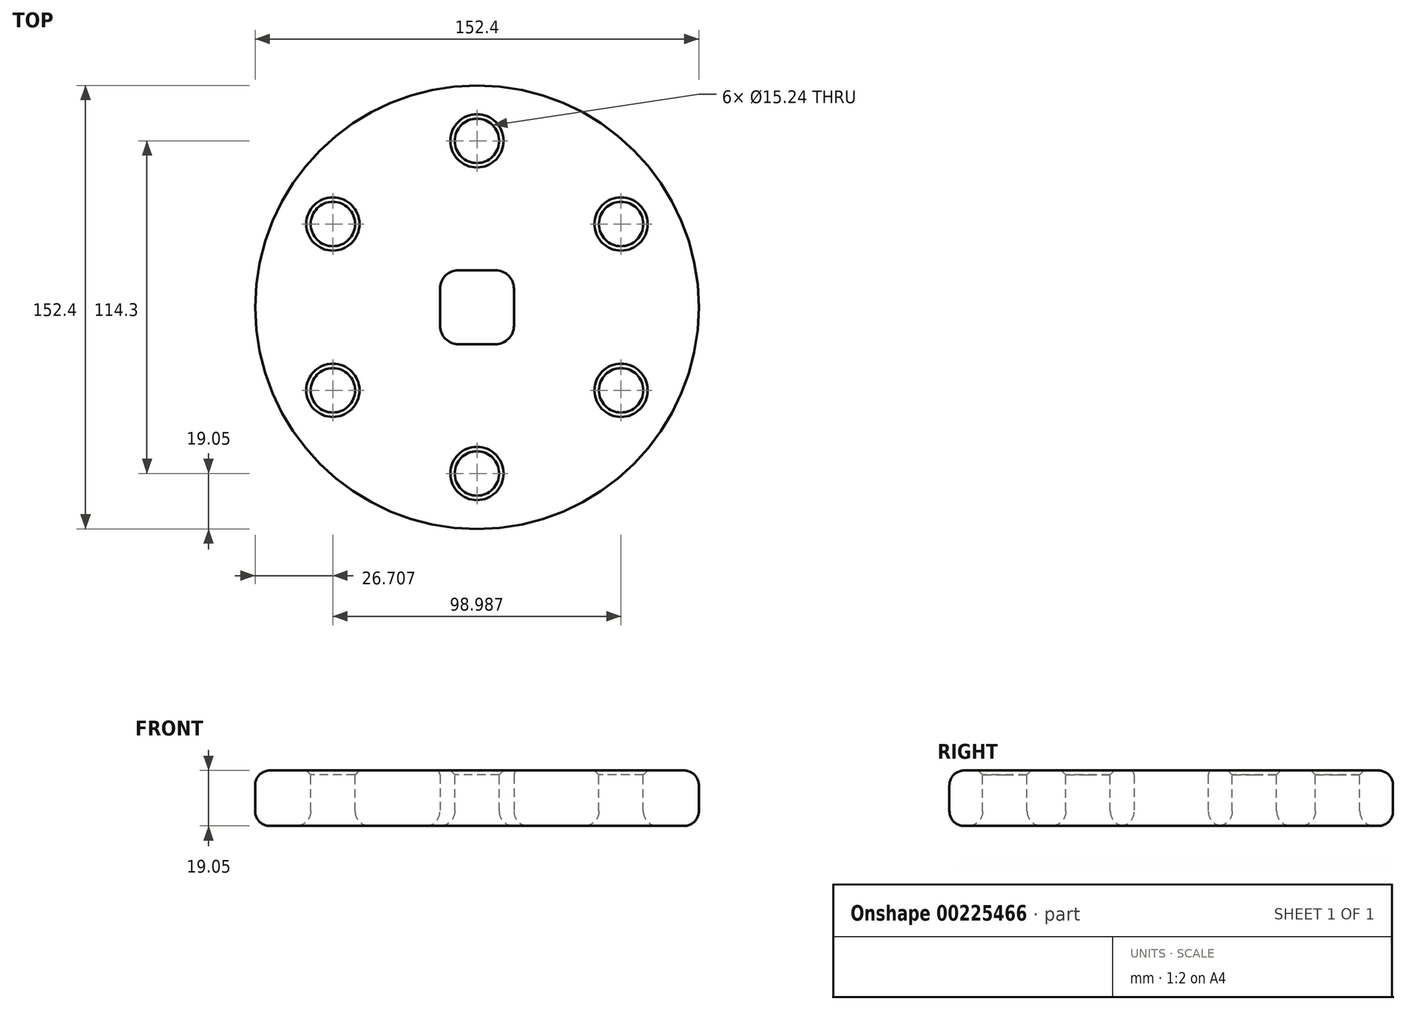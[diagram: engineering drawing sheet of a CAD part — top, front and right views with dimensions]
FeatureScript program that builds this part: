
annotation { "Feature Type Name" : "Feature", "Feature Type Description" : "" }
export const myFeature = defineFeature(function(context is Context, id is Id, definition is map)
    precondition{}
    {
        {
            var Q0;
            Q0=qCreatedBy(makeId("Top.planeOp"),FACE);
            var sketch = newSketch(context, id + "F0", { "sketchPlane" : qUnion([Q0])});
            skCircle(sketch, "E0", {"center": v(0, 0) * mm, "radius": 76.2 * mm});
            skCircle(sketch, "E1", {"center": v(0, 0) * mm, "radius": 57.15 * mm, "construction": true});
            skCircle(sketch, "E2", {"center": v(0, 57.15) * mm, "radius": 7.62 * mm});
            skCircle(sketch, "E3.1.0", {"center": v(-49.5, 28.58) * mm, "radius": 7.62 * mm});
            skCircle(sketch, "E3.2.0", {"center": v(-49.5, -28.57) * mm, "radius": 7.62 * mm});
            skCircle(sketch, "E3.3.0", {"center": v(0, -57.15) * mm, "radius": 7.62 * mm});
            skCircle(sketch, "E3.4.0", {"center": v(49.5, -28.58) * mm, "radius": 7.62 * mm});
            skCircle(sketch, "E3.5.0", {"center": v(49.5, 28.58) * mm, "radius": 7.62 * mm});
            skSolve(sketch);
        }
        {
            var Q0;
            Q0 = qSketchRegion(id + "F0", true);
            extrude(context, id + "F1", {"entities" : qUnion([Q0]), "oppositeDirection" : true, "depth" : 19.05 * mm});
        }
        {
            var Q0;
            Q0=makeQuery(id+"F1.opExtrude","CAP_FACE",FACE,{"disambiguationData":[OSD([sQuery(id+"F0.wireOp",EDGE,"E0"),sQuery(id+"F0.wireOp",EDGE,"E2"),sQuery(id+"F0.wireOp",EDGE,"E3.1.0"),sQuery(id+"F0.wireOp",EDGE,"E3.2.0"),sQuery(id+"F0.wireOp",EDGE,"E3.3.0"),sQuery(id+"F0.wireOp",EDGE,"E3.4.0"),sQuery(id+"F0.wireOp",EDGE,"E3.5.0")])],"isStart":false});
            var sketch = newSketch(context, id + "F2", { "sketchPlane" : qUnion([Q0])});
            skLineSegment(sketch, "E4.bottom", {"start": v(6.35, -12.7) * mm, "end": v(-6.35, -12.7) * mm});
            skLineSegment(sketch, "E4.top", {"start": v(6.35, 12.7) * mm, "end": v(-6.35, 12.7) * mm});
            skLineSegment(sketch, "E4.left", {"start": v(12.7, -6.35) * mm, "end": v(12.7, 6.35) * mm});
            skLineSegment(sketch, "E4.right", {"start": v(-12.7, -6.35) * mm, "end": v(-12.7, 6.35) * mm});
            skPoint(sketch, "E4.middle", {"position": v(0, 0) * mm});
            skPoint(sketch, "E5.visualSharp", {"position": v(-12.7, 12.7) * mm});
            skArc(sketch, "E5.filletArc", {"start": v(-6.35, 12.7) * mm, "mid": v(-10.84, 10.84) * mm, "end": v(-12.7, 6.35) * mm});
            skPoint(sketch, "E6.visualSharp", {"position": v(12.7, 12.7) * mm});
            skArc(sketch, "E6.filletArc", {"start": v(12.7, 6.35) * mm, "mid": v(10.84, 10.84) * mm, "end": v(6.35, 12.7) * mm});
            skPoint(sketch, "E7.visualSharp", {"position": v(12.7, -12.7) * mm});
            skArc(sketch, "E7.filletArc", {"start": v(6.35, -12.7) * mm, "mid": v(10.84, -10.84) * mm, "end": v(12.7, -6.35) * mm});
            skPoint(sketch, "E8.visualSharp", {"position": v(-12.7, -12.7) * mm});
            skArc(sketch, "E8.filletArc", {"start": v(-12.7, -6.35) * mm, "mid": v(-10.84, -10.84) * mm, "end": v(-6.35, -12.7) * mm});
            skSolve(sketch);
        }
        {
            var Q0;
            Q0 = qSketchRegion(id + "F2", true);
            extrude(context, id + "F3", {"entities" : qUnion([Q0]), "operationType" : NewBodyOperationType.REMOVE, "endBound" : BoundingType.THROUGH_ALL, "oppositeDirection" : true, "depth" : 25.4 * mm});
        }
        {
            var Q0;
            Q0=makeQuery(id+"F1.opExtrude","CAP_EDGE",EDGE,{"disambiguationData":[OSD([sQuery(id+"F0.wireOp",EDGE,"E3.1.0")])],"isStart":true});
            var Q1;
            Q1=makeQuery(id+"F1.opExtrude","CAP_EDGE",EDGE,{"disambiguationData":[OSD([sQuery(id+"F0.wireOp",EDGE,"E2")])],"isStart":true});
            var Q2;
            Q2=makeQuery(id+"F1.opExtrude","CAP_EDGE",EDGE,{"disambiguationData":[OSD([sQuery(id+"F0.wireOp",EDGE,"E3.5.0")])],"isStart":true});
            var Q3;
            Q3=makeQuery(id+"F1.opExtrude","CAP_EDGE",EDGE,{"disambiguationData":[OSD([sQuery(id+"F0.wireOp",EDGE,"E3.4.0")])],"isStart":true});
            var Q4;
            Q4=makeQuery(id+"F1.opExtrude","CAP_EDGE",EDGE,{"disambiguationData":[OSD([sQuery(id+"F0.wireOp",EDGE,"E3.3.0")])],"isStart":true});
            var Q5;
            Q5=makeQuery(id+"F1.opExtrude","CAP_EDGE",EDGE,{"disambiguationData":[OSD([sQuery(id+"F0.wireOp",EDGE,"E3.2.0")])],"isStart":true});
            chamfer(context, id + "F4", {"entities" : qUnion([Q0, Q1, Q2, Q3, Q4, Q5]), "width" : 1.52 * mm, "tangentPropagation" : true});
        }
        {
            var Q0;
            Q0=makeQuery(id+"F3.boolean.opBoolean","INTERSECT",EDGE,{"derivedFrom":[makeQuery(id+"F1.opExtrude","CAP_FACE",FACE,{"disambiguationData":[OSD([sQuery(id+"F0.wireOp",EDGE,"E0"),sQuery(id+"F0.wireOp",EDGE,"E2"),sQuery(id+"F0.wireOp",EDGE,"E3.1.0"),sQuery(id+"F0.wireOp",EDGE,"E3.2.0"),sQuery(id+"F0.wireOp",EDGE,"E3.3.0"),sQuery(id+"F0.wireOp",EDGE,"E3.4.0"),sQuery(id+"F0.wireOp",EDGE,"E3.5.0")])],"isStart":true}),makeQuery(id+"F3.opExtrude","SWEPT_FACE",FACE,{"disambiguationData":[OSD([sQuery(id+"F2.wireOp",EDGE,"E4.right")])]})]});
            var Q1;
            Q1=makeQuery(id+"F3.boolean.opBoolean","INTERSECT",EDGE,{"derivedFrom":[makeQuery(id+"F1.opExtrude","CAP_FACE",FACE,{"disambiguationData":[OSD([sQuery(id+"F0.wireOp",EDGE,"E0"),sQuery(id+"F0.wireOp",EDGE,"E2"),sQuery(id+"F0.wireOp",EDGE,"E3.1.0"),sQuery(id+"F0.wireOp",EDGE,"E3.2.0"),sQuery(id+"F0.wireOp",EDGE,"E3.3.0"),sQuery(id+"F0.wireOp",EDGE,"E3.4.0"),sQuery(id+"F0.wireOp",EDGE,"E3.5.0")])],"isStart":true}),makeQuery(id+"F3.opExtrude","SWEPT_FACE",FACE,{"disambiguationData":[OSD([sQuery(id+"F2.wireOp",EDGE,"E8.filletArc")])]})]});
            var Q2;
            Q2=makeQuery(id+"F3.boolean.opBoolean","INTERSECT",EDGE,{"derivedFrom":[makeQuery(id+"F1.opExtrude","CAP_FACE",FACE,{"disambiguationData":[OSD([sQuery(id+"F0.wireOp",EDGE,"E0"),sQuery(id+"F0.wireOp",EDGE,"E2"),sQuery(id+"F0.wireOp",EDGE,"E3.1.0"),sQuery(id+"F0.wireOp",EDGE,"E3.2.0"),sQuery(id+"F0.wireOp",EDGE,"E3.3.0"),sQuery(id+"F0.wireOp",EDGE,"E3.4.0"),sQuery(id+"F0.wireOp",EDGE,"E3.5.0")])],"isStart":true}),makeQuery(id+"F3.opExtrude","SWEPT_FACE",FACE,{"disambiguationData":[OSD([sQuery(id+"F2.wireOp",EDGE,"E4.bottom")])]})]});
            var Q3;
            Q3=makeQuery(id+"F3.boolean.opBoolean","INTERSECT",EDGE,{"derivedFrom":[makeQuery(id+"F1.opExtrude","CAP_FACE",FACE,{"disambiguationData":[OSD([sQuery(id+"F0.wireOp",EDGE,"E0"),sQuery(id+"F0.wireOp",EDGE,"E2"),sQuery(id+"F0.wireOp",EDGE,"E3.1.0"),sQuery(id+"F0.wireOp",EDGE,"E3.2.0"),sQuery(id+"F0.wireOp",EDGE,"E3.3.0"),sQuery(id+"F0.wireOp",EDGE,"E3.4.0"),sQuery(id+"F0.wireOp",EDGE,"E3.5.0")])],"isStart":true}),makeQuery(id+"F3.opExtrude","SWEPT_FACE",FACE,{"disambiguationData":[OSD([sQuery(id+"F2.wireOp",EDGE,"E5.filletArc")])]})]});
            var Q4;
            Q4=makeQuery(id+"F3.boolean.opBoolean","INTERSECT",EDGE,{"derivedFrom":[makeQuery(id+"F1.opExtrude","CAP_FACE",FACE,{"disambiguationData":[OSD([sQuery(id+"F0.wireOp",EDGE,"E0"),sQuery(id+"F0.wireOp",EDGE,"E2"),sQuery(id+"F0.wireOp",EDGE,"E3.1.0"),sQuery(id+"F0.wireOp",EDGE,"E3.2.0"),sQuery(id+"F0.wireOp",EDGE,"E3.3.0"),sQuery(id+"F0.wireOp",EDGE,"E3.4.0"),sQuery(id+"F0.wireOp",EDGE,"E3.5.0")])],"isStart":true}),makeQuery(id+"F3.opExtrude","SWEPT_FACE",FACE,{"disambiguationData":[OSD([sQuery(id+"F2.wireOp",EDGE,"E4.top")])]})]});
            var Q5;
            Q5=makeQuery(id+"F3.boolean.opBoolean","INTERSECT",EDGE,{"derivedFrom":[makeQuery(id+"F1.opExtrude","CAP_FACE",FACE,{"disambiguationData":[OSD([sQuery(id+"F0.wireOp",EDGE,"E0"),sQuery(id+"F0.wireOp",EDGE,"E2"),sQuery(id+"F0.wireOp",EDGE,"E3.1.0"),sQuery(id+"F0.wireOp",EDGE,"E3.2.0"),sQuery(id+"F0.wireOp",EDGE,"E3.3.0"),sQuery(id+"F0.wireOp",EDGE,"E3.4.0"),sQuery(id+"F0.wireOp",EDGE,"E3.5.0")])],"isStart":true}),makeQuery(id+"F3.opExtrude","SWEPT_FACE",FACE,{"disambiguationData":[OSD([sQuery(id+"F2.wireOp",EDGE,"E7.filletArc")])]})]});
            var Q6;
            Q6=makeQuery(id+"F3.boolean.opBoolean","INTERSECT",EDGE,{"derivedFrom":[makeQuery(id+"F1.opExtrude","CAP_FACE",FACE,{"disambiguationData":[OSD([sQuery(id+"F0.wireOp",EDGE,"E0"),sQuery(id+"F0.wireOp",EDGE,"E2"),sQuery(id+"F0.wireOp",EDGE,"E3.1.0"),sQuery(id+"F0.wireOp",EDGE,"E3.2.0"),sQuery(id+"F0.wireOp",EDGE,"E3.3.0"),sQuery(id+"F0.wireOp",EDGE,"E3.4.0"),sQuery(id+"F0.wireOp",EDGE,"E3.5.0")])],"isStart":true}),makeQuery(id+"F3.opExtrude","SWEPT_FACE",FACE,{"disambiguationData":[OSD([sQuery(id+"F2.wireOp",EDGE,"E4.left")])]})]});
            var Q7;
            Q7=makeQuery(id+"F3.boolean.opBoolean","INTERSECT",EDGE,{"derivedFrom":[makeQuery(id+"F1.opExtrude","CAP_FACE",FACE,{"disambiguationData":[OSD([sQuery(id+"F0.wireOp",EDGE,"E0"),sQuery(id+"F0.wireOp",EDGE,"E2"),sQuery(id+"F0.wireOp",EDGE,"E3.1.0"),sQuery(id+"F0.wireOp",EDGE,"E3.2.0"),sQuery(id+"F0.wireOp",EDGE,"E3.3.0"),sQuery(id+"F0.wireOp",EDGE,"E3.4.0"),sQuery(id+"F0.wireOp",EDGE,"E3.5.0")])],"isStart":true}),makeQuery(id+"F3.opExtrude","SWEPT_FACE",FACE,{"disambiguationData":[OSD([sQuery(id+"F2.wireOp",EDGE,"E6.filletArc")])]})]});
            fillet(context, id + "F5", {"entities" : qUnion([Q0, Q1, Q2, Q3, Q4, Q5, Q6, Q7]), "radius" : 1.52 * mm, "tangentPropagation" : true, "allowEdgeOverflow" : false});
        }
        {
            var Q0;
            Q0=makeQuery(id+"F1.opExtrude","CAP_FACE",FACE,{"disambiguationData":[OSD([sQuery(id+"F0.wireOp",EDGE,"E0"),sQuery(id+"F0.wireOp",EDGE,"E2"),sQuery(id+"F0.wireOp",EDGE,"E3.1.0"),sQuery(id+"F0.wireOp",EDGE,"E3.2.0"),sQuery(id+"F0.wireOp",EDGE,"E3.3.0"),sQuery(id+"F0.wireOp",EDGE,"E3.4.0"),sQuery(id+"F0.wireOp",EDGE,"E3.5.0")])],"isStart":false});
            fillet(context, id + "F6", {"entities" : qUnion([Q0]), "radius" : 5.08 * mm, "tangentPropagation" : true, "allowEdgeOverflow" : false});
        }
        {
            var Q0;
            Q0=makeQuery(id+"F1.opExtrude","CAP_FACE",FACE,{"disambiguationData":[OSD([sQuery(id+"F0.wireOp",EDGE,"E0"),sQuery(id+"F0.wireOp",EDGE,"E2"),sQuery(id+"F0.wireOp",EDGE,"E3.1.0"),sQuery(id+"F0.wireOp",EDGE,"E3.2.0"),sQuery(id+"F0.wireOp",EDGE,"E3.3.0"),sQuery(id+"F0.wireOp",EDGE,"E3.4.0"),sQuery(id+"F0.wireOp",EDGE,"E3.5.0")])],"isStart":false});
            var Q1;
            Q1=makeQuery(id+"F1.opExtrude","CAP_EDGE",EDGE,{"disambiguationData":[OSD([sQuery(id+"F0.wireOp",EDGE,"E0")])],"isStart":true});
            fillet(context, id + "F7", {"entities" : qUnion([Q0, Q1]), "radius" : 5.08 * mm, "tangentPropagation" : true, "allowEdgeOverflow" : false});
        }
    });
